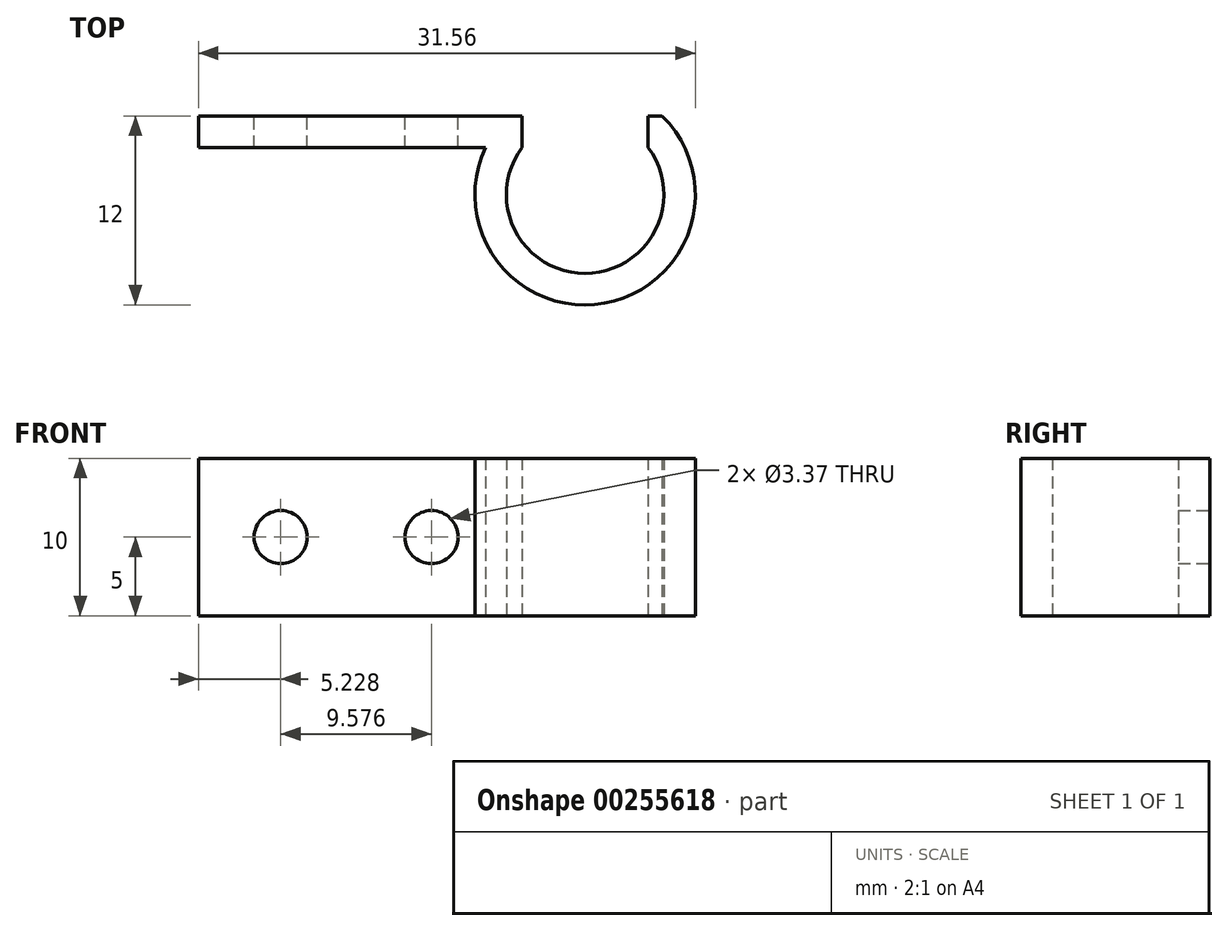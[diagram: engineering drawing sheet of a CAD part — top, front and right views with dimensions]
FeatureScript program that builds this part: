
annotation { "Feature Type Name" : "Feature", "Feature Type Description" : "" }
export const myFeature = defineFeature(function(context is Context, id is Id, definition is map)
    precondition{}
    {
        {
            var Q0;
            Q0=qCreatedBy(makeId("Top.planeOp"),FACE);
            var sketch = newSketch(context, id + "F0", { "sketchPlane" : qUnion([Q0])});
            skArc(sketch, "E0", {"start": v(-4, 3) * mm, "mid": v(0, -5) * mm, "end": v(4, 3) * mm});
            skArc(sketch, "E1", {"start": v(-6.32, 3) * mm, "mid": v(1.23, -6.9) * mm, "end": v(4.9, 5) * mm});
            skLineSegment(sketch, "E2.left", {"start": v(-4, 5) * mm, "end": v(-4, 3) * mm});
            skLineSegment(sketch, "E2.right", {"start": v(4, 5) * mm, "end": v(4, 3) * mm});
            skLineSegment(sketch, "E3", {"start": v(0, 0) * mm, "end": v(0, 36.4) * mm, "construction": true});
            skLineSegment(sketch, "E4", {"start": v(-24.56, 5) * mm, "end": v(-4, 5) * mm});
            skLineSegment(sketch, "E5.trimOffspring", {"start": v(4, 5) * mm, "end": v(4.9, 5) * mm});
            skLineSegment(sketch, "E6", {"start": v(-24.56, 5) * mm, "end": v(-24.56, 3) * mm});
            skLineSegment(sketch, "E7", {"start": v(-24.56, 3) * mm, "end": v(-6.32, 3) * mm});
            skArc(sketch, "E8", {"start": v(4, 3) * mm, "mid": v(0, 5) * mm, "end": v(-4, 3) * mm, "construction": true});
            skSolve(sketch);
        }
        {
            var Q0;
            Q0 = qSketchRegion(id + "F0", true);
            extrude(context, id + "F1", {"entities" : qUnion([Q0]), "endBound" : BoundingType.SYMMETRIC, "depth" : 10 * mm});
        }
        {
            var Q0;
            Q0=makeQuery(id+"F1.opExtrude","SWEPT_FACE",FACE,{"disambiguationData":[OSD([sQuery(id+"F0.wireOp",EDGE,"E4")])]});
            var sketch = newSketch(context, id + "F2", { "sketchPlane" : qUnion([Q0])});
            skCircle(sketch, "E9", {"center": v(19.33, 0) * mm, "radius": 1.44 * mm, "construction": true});
            skCircle(sketch, "E10", {"center": v(9.76, 0) * mm, "radius": 1.44 * mm, "construction": true});
            skLineSegment(sketch, "E11.bottom", {"start": v(0, 0) * mm, "end": v(24.56, 0) * mm, "construction": true});
            skLineSegment(sketch, "E11.top", {"start": v(0, 5) * mm, "end": v(24.56, 5) * mm, "construction": true});
            skLineSegment(sketch, "E11.left", {"start": v(0, 0) * mm, "end": v(0, 5) * mm, "construction": true});
            skLineSegment(sketch, "E11.right", {"start": v(24.56, 0) * mm, "end": v(24.56, 5) * mm, "construction": true});
            skCircle(sketch, "E12", {"center": v(19.33, 0) * mm, "radius": 1.69 * mm});
            skCircle(sketch, "E13", {"center": v(9.76, 0) * mm, "radius": 1.69 * mm});
            skLineSegment(sketch, "E14", {"start": v(7, 0) * mm, "end": v(7, 5) * mm, "construction": true});
            skCircle(sketch, "E15", {"center": v(9.76, 0) * mm, "radius": 2.76 * mm, "construction": true});
            skSolve(sketch);
        }
        {
            var Q0;
            Q0 = qSketchRegion(id + "F2", true);
            extrude(context, id + "F3", {"entities" : qUnion([Q0]), "operationType" : NewBodyOperationType.REMOVE, "endBound" : BoundingType.THROUGH_ALL, "oppositeDirection" : true, "depth" : 25 * mm});
        }
    });
